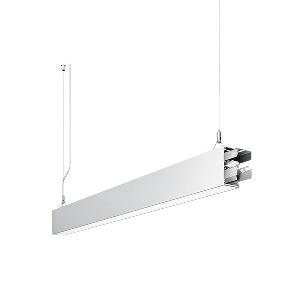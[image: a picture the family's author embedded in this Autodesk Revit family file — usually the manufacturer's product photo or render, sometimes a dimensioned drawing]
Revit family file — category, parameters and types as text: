
# Revit family: idoo_line_-_ilp_4000_vtl_d_sta_00806453_76da
name_source: partatom
category: Lighting Fixtures
units: mm (PartAtom-declared; Revit-internal decimal feet)

## family parameters
Cut with Voids When Loaded = No
Host = Face
Light Source = No
Part Type = Normal
Room Calculation Point = No
Round Connector Dimension = Use Diameter
Shared = No

## types (1)
- IDOO.line - ILP 4000/VTL/D STA (1 x LED, 3850 lm, 2700-6500K)
    Apparent Load = 39 VA
    Approval mark = CE
    CIE Flux Codes = 66 91 98 40 100
    Color Rendering = 90-100
    Color Temperature = 2700-6500K
    Control Gear = Electronic ballast
    Default Elevation = 1800 mm
    Description = ILP 4000/VTL/D|Suspended luminaire|light source: LED|connected load: 220-240 V, 50/60 Hz|Power consumption: approx. 39 W|standby: approx. 0,25|luminous flux: 3850 lm|luminous efficacy: 98 lm/W|light distribution: Direct/indirect|direct ratio: approx. 40 %|colour temperature: Cold white, ca. 2700-6500 K|color rendering index (CRI): >= 90|chromaticity tolerance:  3 SDCM|System of protection: IP 40|technology: Continuously dimmable|luminaire body|material: Sectional aluminium|colour: White|lamp cover: Acrylic (PMMA), Clear|mains lead: 2.00 m With free stranded wires|Fastening: Steel cable 0.3 - 0.7 m|glare control: Prism aperture|luminance(L65): <= 2700 cd/m|unified glare rating(4H 8H): <=  16|special features: Specified values at approx. 4000 K, DALI Load 1x, Through-wired, up to 18 m on one mains connection, External control required for Dali Device type 8, Flicker-free, Constant luminous flux between 2700 and 6500 K, Constant colour temperature over the whole dimming range, Suitable as emergency lighting, Start luminaire with mains connection, Mechanical and electrical connection of the individual modules without tools|
    Frequency = 50 Hz
    Height = 110 mm
    Lamp = 1 x LED
    Lamp Light Flux = 3850 lm
    Lamp count = 1
    Length = 1408 mm
    Luminous efficacy = 99 lm/W
    Manufacturer = Waldmann
    ModVariant = No
    Model = 00806453
    Mounting Place = Ceiling
    Mounting Type = Pendant
    Number of Poles = 1
    OnlyDefault = Yes
    Power Factor = 1
    Product Name = IDOO.line - ILP 4000/VTL/D STA
    Product group = Suspended luminaire
    ProductGroupID = 9
    Protection Class = Protection class I
    Protection Degree = IP 40
    RLX_Detail_Level = 1
    RLX_Emergency_Light_Flux = 0 lm
    RLX_Emergency_Type = 0
    RLX_Emergency_Type_DB = No
    RlxData = <blob elided: 22345 chars, md5=ae5a9caf>
    Socket = socket
    Standby Power = 0 W
    System Light Flux = 3850 lm
    System Power = 39 W
    Type Comments = Product without accessories
    Type Image = 113307000-00692585.jpg
    URL = http://relux.com
    VarID = ---
    Voltage = 230 V
    Voltage Range = 220-240 V
    Weight = 0.00 kg
    Width = 60 mm  [stored 0.19685 ft]

note: [stored X ft] marks values corroborated as IEEE doubles in the binary element streams (Revit-internal decimal feet)

## geometry (parser evidence)
native form markers: Blend x4, Sweep x13
no freeform markers — native parametric forms only
